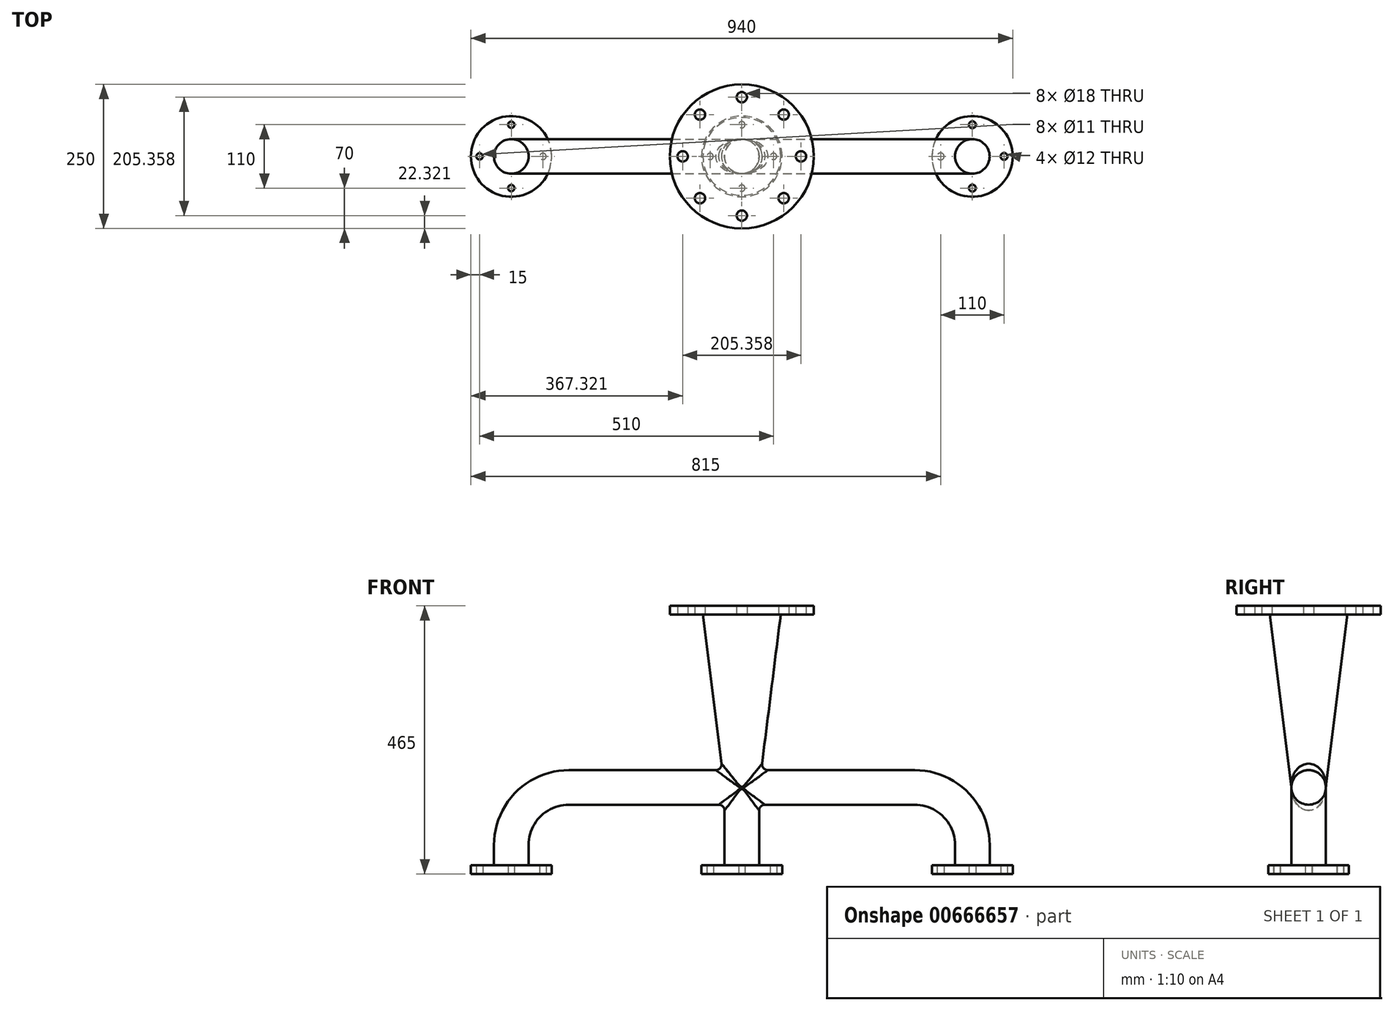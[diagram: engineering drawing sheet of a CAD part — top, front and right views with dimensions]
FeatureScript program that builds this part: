
annotation { "Feature Type Name" : "Feature", "Feature Type Description" : "" }
export const myFeature = defineFeature(function(context is Context, id is Id, definition is map)
    precondition{}
    {
        {
            var Q0;
            Q0=qCreatedBy(makeId("Front.planeOp"),FACE);
            var sketch = newSketch(context, id + "F0", { "sketchPlane" : qUnion([Q0])});
            skLineSegment(sketch, "E0", {"start": v(0, 0) * mm, "end": v(300, 0) * mm});
            skLineSegment(sketch, "E1", {"start": v(0, 0) * mm, "end": v(-300, 0) * mm});
            skLineSegment(sketch, "E2", {"start": v(0, 0) * mm, "end": v(0, 300) * mm});
            skLineSegment(sketch, "E3", {"start": v(-400, -100) * mm, "end": v(-400, -150) * mm});
            skLineSegment(sketch, "E4", {"start": v(0, 0) * mm, "end": v(0, -150) * mm});
            skLineSegment(sketch, "E5", {"start": v(400, -100) * mm, "end": v(400, -150) * mm});
            skPoint(sketch, "E6.visualSharp", {"position": v(-400, 0) * mm});
            skArc(sketch, "E6.filletArc", {"start": v(-300, 0) * mm, "mid": v(-370.71, -29.29) * mm, "end": v(-400, -100) * mm});
            skPoint(sketch, "E7.visualSharp", {"position": v(400, 0) * mm});
            skArc(sketch, "E7.filletArc", {"start": v(400, -100) * mm, "mid": v(370.71, -29.29) * mm, "end": v(300, 0) * mm});
            skSolve(sketch);
        }
        {
            var Q0;
            Q0=qCreatedBy(makeId("Top.planeOp"),FACE);
            cPlane(context, id + "F1", {"entities" : qUnion([Q0]), "cplaneType" : CPlaneType.OFFSET, "offset" : 300 * mm, "width" : 150 * mm, "height" : 150 * mm});
        }
        {
            var Q0;
            Q0=qCreatedBy(id+"F1.planeOp",FACE);
            var sketch = newSketch(context, id + "F2", { "sketchPlane" : qUnion([Q0])});
            skPoint(sketch, "E8.0", {"position": v(0, 0) * mm});
            skCircle(sketch, "E9", {"center": v(0, 0) * mm, "radius": 125 * mm});
            skCircle(sketch, "E10", {"center": v(0, 0) * mm, "radius": 67.5 * mm});
            skCircle(sketch, "E11", {"center": v(0, 102.68) * mm, "radius": 9 * mm});
            skCircle(sketch, "E12.1.0", {"center": v(-72.6, 72.6) * mm, "radius": 9 * mm});
            skCircle(sketch, "E12.2.0", {"center": v(-102.68, 0) * mm, "radius": 9 * mm});
            skCircle(sketch, "E12.3.0", {"center": v(-72.6, -72.6) * mm, "radius": 9 * mm});
            skCircle(sketch, "E12.4.0", {"center": v(0, -102.68) * mm, "radius": 9 * mm});
            skCircle(sketch, "E12.5.0", {"center": v(72.6, -72.6) * mm, "radius": 9 * mm});
            skCircle(sketch, "E12.6.0", {"center": v(102.68, 0) * mm, "radius": 9 * mm});
            skCircle(sketch, "E12.7.0", {"center": v(72.6, 72.6) * mm, "radius": 9 * mm});
            skSolve(sketch);
        }
        {
            var Q0;
            Q0=qCreatedBy(makeId("Top.planeOp"),FACE);
            cPlane(context, id + "F3", {"entities" : qUnion([Q0]), "cplaneType" : CPlaneType.OFFSET, "offset" : 150 * mm, "oppositeDirection" : true, "width" : 150 * mm, "height" : 150 * mm});
        }
        {
            var Q0;
            Q0=qCreatedBy(makeId("Top.planeOp"),FACE);
            var sketch = newSketch(context, id + "F4", { "sketchPlane" : qUnion([Q0])});
            skCircle(sketch, "E13", {"center": v(0, 0) * mm, "radius": 30 * mm});
            skSolve(sketch);
        }
        {
            var Q0;
            Q0=qCreatedBy(id+"F3.planeOp",FACE);
            var sketch = newSketch(context, id + "F5", { "sketchPlane" : qUnion([Q0])});
            skPoint(sketch, "E14.0", {"position": v(0, 0) * mm});
            skPoint(sketch, "E15.0", {"position": v(-400, 0) * mm});
            skPoint(sketch, "E16.0", {"position": v(400, 0) * mm});
            skCircle(sketch, "E17", {"center": v(0, 0) * mm, "radius": 30 * mm});
            skCircle(sketch, "E18", {"center": v(0, 0) * mm, "radius": 70 * mm});
            skCircle(sketch, "E19", {"center": v(-400, 0) * mm, "radius": 30 * mm});
            skCircle(sketch, "E20", {"center": v(-400, 0) * mm, "radius": 70 * mm});
            skCircle(sketch, "E21", {"center": v(400, 0) * mm, "radius": 30 * mm});
            skCircle(sketch, "E22", {"center": v(400, 0) * mm, "radius": 70 * mm});
            skCircle(sketch, "E23", {"center": v(-400, -55) * mm, "radius": 5.5 * mm});
            skCircle(sketch, "E24.1.0", {"center": v(-345, 0) * mm, "radius": 5.5 * mm});
            skCircle(sketch, "E24.2.0", {"center": v(-400, 55) * mm, "radius": 5.5 * mm});
            skCircle(sketch, "E24.3.0", {"center": v(-455, 0) * mm, "radius": 5.5 * mm});
            skCircle(sketch, "E25", {"center": v(55, 0) * mm, "radius": 5.5 * mm});
            skCircle(sketch, "E26.1.0", {"center": v(0, 55) * mm, "radius": 5.5 * mm});
            skCircle(sketch, "E26.2.0", {"center": v(-55, 0) * mm, "radius": 5.5 * mm});
            skCircle(sketch, "E26.3.0", {"center": v(0, -55) * mm, "radius": 5.5 * mm});
            skCircle(sketch, "E27", {"center": v(455, 0) * mm, "radius": 6 * mm});
            skCircle(sketch, "E28.1.0", {"center": v(400, 55) * mm, "radius": 6 * mm});
            skCircle(sketch, "E28.2.0", {"center": v(345, 0) * mm, "radius": 6 * mm});
            skCircle(sketch, "E28.3.0", {"center": v(400, -55) * mm, "radius": 6 * mm});
            skSolve(sketch);
        }
        {
            var Q0;
            Q0=makeQuery(id+"F5.imprint","IMPRINT",FACE,{"disambiguationData":[TD([[makeQuery(id+"F5.imprint","IMPRINT",EDGE,{"derivedFrom":sQuery(id+"F5.wireOp",EDGE,"E19")}),1.0]])]});
            var Q1;
            Q1=sQuery(id+"F0.wireOp",EDGE,"E3");
            var Q2;
            Q2=sQuery(id+"F0.wireOp",EDGE,"E6.filletArc");
            var Q3;
            Q3=sQuery(id+"F0.wireOp",EDGE,"E1");
            sweep(context, id + "F6", {"profiles" : qUnion([Q0]), "path" : qUnion([Q1, Q2, Q3])});
        }
        {
            var Q0;
            Q0=makeQuery(id+"F5.imprint","IMPRINT",FACE,{"disambiguationData":[TD([[makeQuery(id+"F5.imprint","IMPRINT",EDGE,{"derivedFrom":sQuery(id+"F5.wireOp",EDGE,"E21")}),1.0]])]});
            var Q1;
            Q1=sQuery(id+"F0.wireOp",EDGE,"E5");
            var Q2;
            Q2=sQuery(id+"F0.wireOp",EDGE,"E7.filletArc");
            var Q3;
            Q3=sQuery(id+"F0.wireOp",EDGE,"E0");
            sweep(context, id + "F7", {"operationType" : NewBodyOperationType.ADD, "profiles" : qUnion([Q0]), "path" : qUnion([Q1, Q2, Q3])});
        }
        {
            var Q0;
            Q0=makeQuery(id+"F5.imprint","IMPRINT",FACE,{"disambiguationData":[TD([[makeQuery(id+"F5.imprint","IMPRINT",EDGE,{"derivedFrom":sQuery(id+"F5.wireOp",EDGE,"E17")}),1.0]])]});
            var Q1;
            Q1=sQuery(id+"F0.wireOp",EDGE,"E4");
            sweep(context, id + "F8", {"operationType" : NewBodyOperationType.ADD, "profiles" : qUnion([Q0]), "path" : qUnion([Q1])});
        }
        {
            var Q1;
            Q1 = qSketchRegion(id + "F4", true);
            var Q2;
            Q2=makeQuery(id+"F2.imprint","IMPRINT",FACE,{"disambiguationData":[TD([[makeQuery(id+"F2.imprint","IMPRINT",EDGE,{"derivedFrom":sQuery(id+"F2.wireOp",EDGE,"E10")}),1.0]])]});
            loft(context, id + "F9", {"operationType" : NewBodyOperationType.ADD, "sheetProfilesArray" : [{ "sheetProfileEntities" : qUnion([Q1]) }, { "sheetProfileEntities" : qUnion([Q2]) }]});
        }
        {
            var Q0;
            Q0=makeQuery(id+"F2.imprint","IMPRINT",FACE,{"disambiguationData":[TD([[makeQuery(id+"F2.imprint","IMPRINT",EDGE,{"derivedFrom":sQuery(id+"F2.wireOp",EDGE,"E9")}),1.0]])]});
            var Q1;
            Q1=makeQuery(id+"F5.imprint","IMPRINT",FACE,{"disambiguationData":[TD([[makeQuery(id+"F5.imprint","IMPRINT",EDGE,{"derivedFrom":sQuery(id+"F5.wireOp",EDGE,"E21")}),-1.0]])]});
            var Q2;
            Q2=makeQuery(id+"F5.imprint","IMPRINT",FACE,{"disambiguationData":[TD([[makeQuery(id+"F5.imprint","IMPRINT",EDGE,{"derivedFrom":sQuery(id+"F5.wireOp",EDGE,"E17")}),-1.0]])]});
            var Q3;
            Q3=makeQuery(id+"F5.imprint","IMPRINT",FACE,{"disambiguationData":[TD([[makeQuery(id+"F5.imprint","IMPRINT",EDGE,{"derivedFrom":sQuery(id+"F5.wireOp",EDGE,"E19")}),-1.0]])]});
            var Q4;
            Q4=makeQuery(id+"F2.imprint","IMPRINT",FACE,{"disambiguationData":[TD([[makeQuery(id+"F2.imprint","IMPRINT",EDGE,{"derivedFrom":sQuery(id+"F2.wireOp",EDGE,"E10")}),1.0]])]});
            var Q5;
            Q5=makeQuery(id+"F5.imprint","IMPRINT",FACE,{"disambiguationData":[TD([[makeQuery(id+"F5.imprint","IMPRINT",EDGE,{"derivedFrom":sQuery(id+"F5.wireOp",EDGE,"E17")}),1.0]])]});
            var Q6;
            Q6=makeQuery(id+"F5.imprint","IMPRINT",FACE,{"disambiguationData":[TD([[makeQuery(id+"F5.imprint","IMPRINT",EDGE,{"derivedFrom":sQuery(id+"F5.wireOp",EDGE,"E21")}),1.0]])]});
            var Q7;
            Q7=makeQuery(id+"F5.imprint","IMPRINT",FACE,{"disambiguationData":[TD([[makeQuery(id+"F5.imprint","IMPRINT",EDGE,{"derivedFrom":sQuery(id+"F5.wireOp",EDGE,"E19")}),1.0]])]});
            extrude(context, id + "F10", {"entities" : qUnion([Q0, Q1, Q2, Q3, Q4, Q5, Q6, Q7]), "operationType" : NewBodyOperationType.ADD, "depth" : 15 * mm, "offsetDistance" : 25 * mm});
        }
        {
            var Q0;
            Q0=makeQuery(id+"F9.boolean.opBoolean","INTERSECT",EDGE,{"disambiguationData":[OD(1.0)],"derivedFrom":[makeQuery(id+"F7.boolean.opBoolean","MERGE",FACE,{"derivedFrom":[makeQuery(id+"F6.opSweep","SWEPT_FACE",FACE,{"disambiguationData":[OSD([sQuery(id+"F0.wireOp",EDGE,"E1"),sQuery(id+"F5.wireOp",EDGE,"E19")])]}),makeQuery(id+"F7.opSweep","SWEPT_FACE",FACE,{"disambiguationData":[OSD([sQuery(id+"F0.wireOp",EDGE,"E0"),sQuery(id+"F5.wireOp",EDGE,"E21")])]})]}),makeQuery(id+"F9.opLoft","SWEPT_FACE",FACE,{"disambiguationData":[OSD([sQuery(id+"F2.wireOp",EDGE,"E10"),sQuery(id+"F4.wireOp",EDGE,"E13")])]})]});
            var Q1;
            Q1=makeQuery(id+"F9.boolean.opBoolean","INTERSECT",EDGE,{"disambiguationData":[OD(0.0)],"derivedFrom":[makeQuery(id+"F7.boolean.opBoolean","MERGE",FACE,{"derivedFrom":[makeQuery(id+"F6.opSweep","SWEPT_FACE",FACE,{"disambiguationData":[OSD([sQuery(id+"F0.wireOp",EDGE,"E1"),sQuery(id+"F5.wireOp",EDGE,"E19")])]}),makeQuery(id+"F7.opSweep","SWEPT_FACE",FACE,{"disambiguationData":[OSD([sQuery(id+"F0.wireOp",EDGE,"E0"),sQuery(id+"F5.wireOp",EDGE,"E21")])]})]}),makeQuery(id+"F9.opLoft","SWEPT_FACE",FACE,{"disambiguationData":[OSD([sQuery(id+"F2.wireOp",EDGE,"E10"),sQuery(id+"F4.wireOp",EDGE,"E13")])]})]});
            fillet(context, id + "F11", {"entities" : qUnion([Q0, Q1]), "radius" : 10 * mm, "tangentPropagation" : true, "allowEdgeOverflow" : false});
        }
        {
            var Q0;
            Q0=makeQuery(id+"F8.boolean.opBoolean","INTERSECT",EDGE,{"disambiguationData":[OD(1.0)],"derivedFrom":[makeQuery(id+"F7.boolean.opBoolean","MERGE",FACE,{"derivedFrom":[makeQuery(id+"F6.opSweep","SWEPT_FACE",FACE,{"disambiguationData":[OSD([sQuery(id+"F0.wireOp",EDGE,"E1"),sQuery(id+"F5.wireOp",EDGE,"E19")])]}),makeQuery(id+"F7.opSweep","SWEPT_FACE",FACE,{"disambiguationData":[OSD([sQuery(id+"F0.wireOp",EDGE,"E0"),sQuery(id+"F5.wireOp",EDGE,"E21")])]})]}),makeQuery(id+"F8.opSweep","SWEPT_FACE",FACE,{"disambiguationData":[OSD([sQuery(id+"F0.wireOp",EDGE,"E4"),sQuery(id+"F5.wireOp",EDGE,"E17")])]})]});
            var Q1;
            Q1=makeQuery(id+"F8.boolean.opBoolean","INTERSECT",EDGE,{"disambiguationData":[OD(0.0)],"derivedFrom":[makeQuery(id+"F7.boolean.opBoolean","MERGE",FACE,{"derivedFrom":[makeQuery(id+"F6.opSweep","SWEPT_FACE",FACE,{"disambiguationData":[OSD([sQuery(id+"F0.wireOp",EDGE,"E1"),sQuery(id+"F5.wireOp",EDGE,"E19")])]}),makeQuery(id+"F7.opSweep","SWEPT_FACE",FACE,{"disambiguationData":[OSD([sQuery(id+"F0.wireOp",EDGE,"E0"),sQuery(id+"F5.wireOp",EDGE,"E21")])]})]}),makeQuery(id+"F8.opSweep","SWEPT_FACE",FACE,{"disambiguationData":[OSD([sQuery(id+"F0.wireOp",EDGE,"E4"),sQuery(id+"F5.wireOp",EDGE,"E17")])]})]});
            fillet(context, id + "F12", {"entities" : qUnion([Q0, Q1]), "radius" : 10 * mm, "tangentPropagation" : true, "allowEdgeOverflow" : false});
        }
    });
